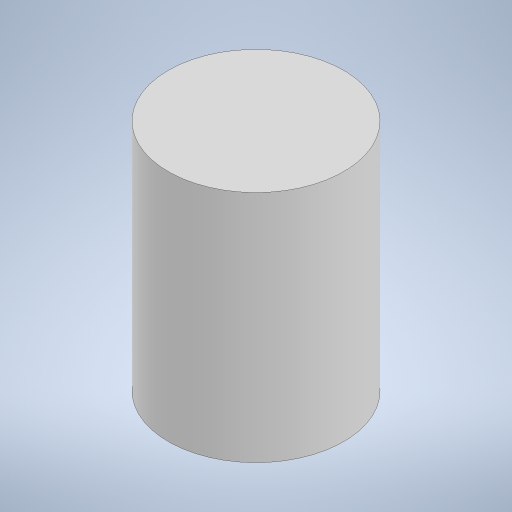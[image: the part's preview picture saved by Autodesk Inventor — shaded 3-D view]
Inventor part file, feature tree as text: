
AUTODESK INVENTOR PART (.ipt)
format: ipt  version: 2023 (Build 270158000, 158)  size: 189,440 bytes
history: native  units: mm
features: extrude x1, sketch x1
ambient origin geometry x8: Origin, YZ Plane, XZ Plane, XY Plane, X Axis, Y Axis, Z Axis, Center Point
bodies: Solid1 (feature_tree)
feature tree (2):
  extrude  "Extrusion1"  Depth=20.0mm TaperAngle=0.0deg
  sketch  "Sketch1"  dims[d0=15.0mm d1=20.0mm d2=0.0mm]
